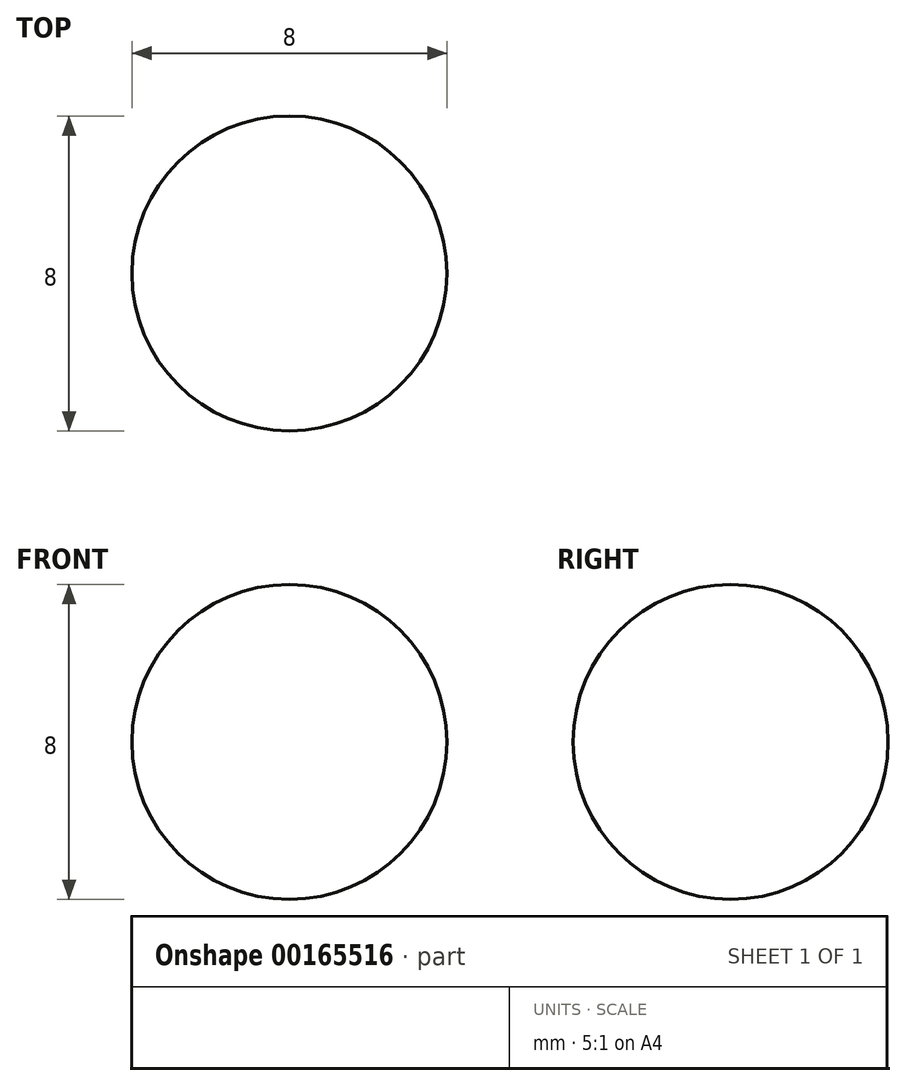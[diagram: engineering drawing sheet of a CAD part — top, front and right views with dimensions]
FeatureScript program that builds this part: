
annotation { "Feature Type Name" : "Feature", "Feature Type Description" : "" }
export const myFeature = defineFeature(function(context is Context, id is Id, definition is map)
    precondition{}
    {
        {
            var Q0;
            Q0=qCreatedBy(makeId("Top.planeOp"),FACE);
            var sketch = newSketch(context, id + "F0", { "sketchPlane" : qUnion([Q0])});
            skArc(sketch, "E0", {"start": v(-47.73, 5.65) * mm, "mid": v(-51.73, 1.65) * mm, "end": v(-47.73, -2.35) * mm});
            skLineSegment(sketch, "E1", {"start": v(-47.73, 5.65) * mm, "end": v(-47.73, 1.65) * mm});
            skLineSegment(sketch, "E2", {"start": v(-47.73, 1.65) * mm, "end": v(-47.73, -2.35) * mm});
            skSolve(sketch);
        }
        {
            var Q0;
            Q0=makeQuery(id+"F0.imprint","IMPRINT",FACE,{"disambiguationData":[TD([[makeQuery(id+"F0.imprint","IMPRINT",EDGE,{"derivedFrom":sQuery(id+"F0.wireOp",EDGE,"E0")}),1.0]])]});
            var Q1;
            Q1=sQuery(id+"F0.wireOp",EDGE,"E1");
            revolve(context, id + "F1", {"entities" : qUnion([Q0]), "axis" : qUnion([Q1]), "revolveType" : RevolveType.FULL});
        }
    });
